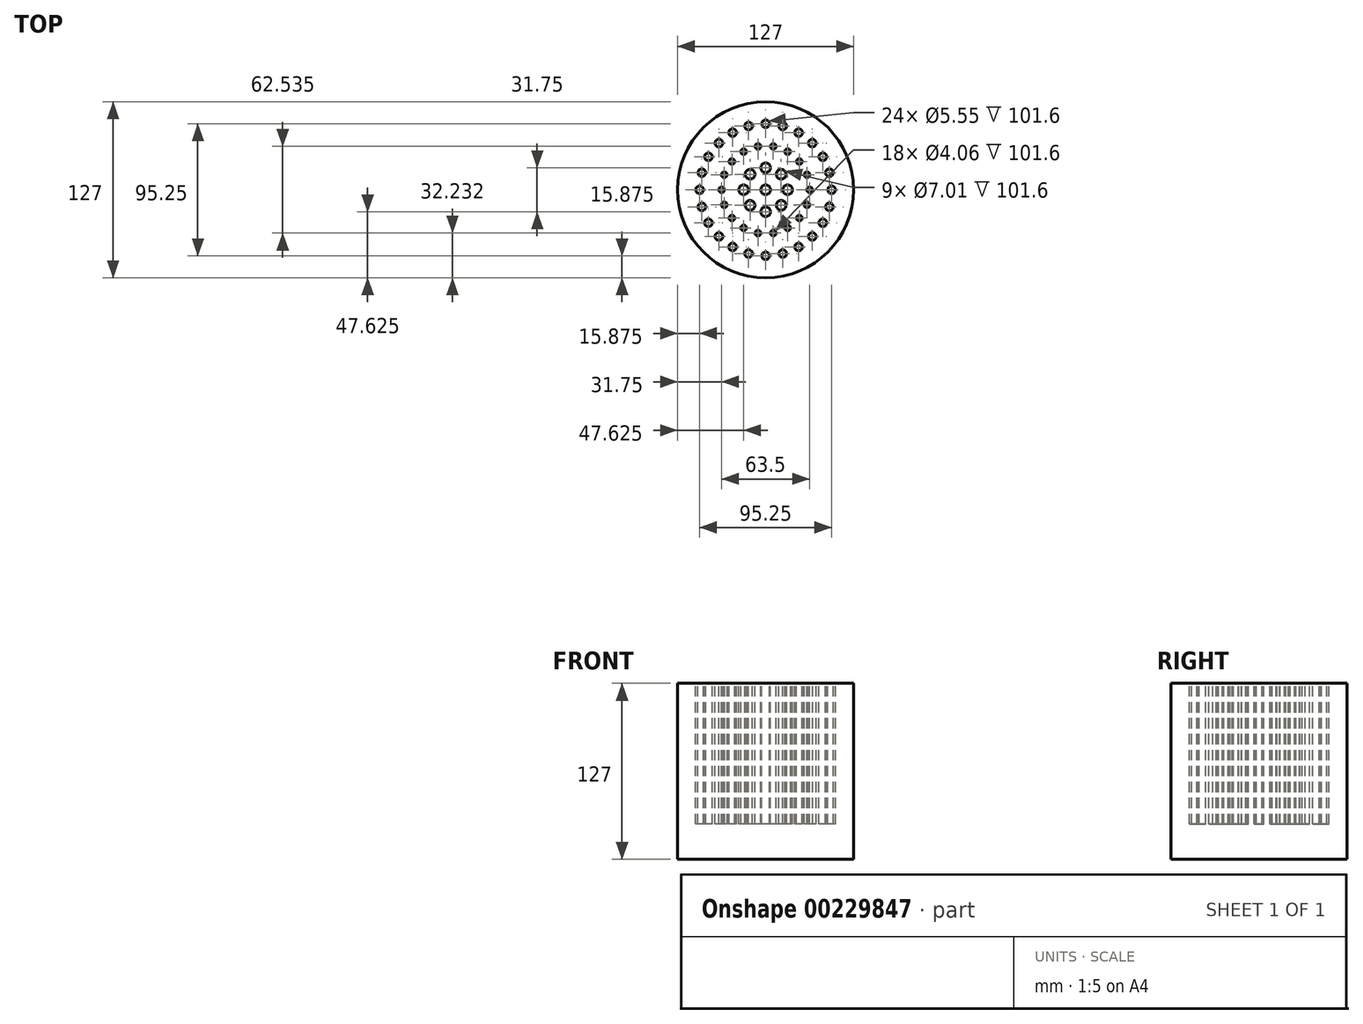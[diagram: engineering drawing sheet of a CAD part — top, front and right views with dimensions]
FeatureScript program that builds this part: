
annotation { "Feature Type Name" : "Feature", "Feature Type Description" : "" }
export const myFeature = defineFeature(function(context is Context, id is Id, definition is map)
    precondition{}
    {
        {
            var Q0;
            Q0=qCreatedBy(makeId("Top.planeOp"),FACE);
            var sketch = newSketch(context, id + "F0", { "sketchPlane" : qUnion([Q0])});
            skCircle(sketch, "E0", {"center": v(0, 0) * mm, "radius": 63.5 * mm});
            skSolve(sketch);
        }
        {
            var Q0;
            Q0 = qSketchRegion(id + "F0", true);
            extrude(context, id + "F1", {"entities" : qUnion([Q0]), "endBound" : BoundingType.SYMMETRIC, "depth" : 127 * mm});
        }
        {
            var Q0;
            Q0=makeQuery(id+"F1.opExtrude","CAP_FACE",FACE,{"disambiguationData":[OSD([sQuery(id+"F0.wireOp",EDGE,"E0")])],"isStart":false});
            var sketch = newSketch(context, id + "F2", { "sketchPlane" : qUnion([Q0])});
            skCircle(sketch, "E1", {"center": v(0, 0) * mm, "radius": 3.5 * mm});
            skLineSegment(sketch, "E2", {"start": v(0, 0) * mm, "end": v(-15.88, 0) * mm});
            skLineSegment(sketch, "E3", {"start": v(-15.88, 0) * mm, "end": v(-31.75, 0) * mm});
            skLineSegment(sketch, "E4", {"start": v(-31.75, 0) * mm, "end": v(-47.62, 0) * mm});
            skCircle(sketch, "E5", {"center": v(-47.62, 0) * mm, "radius": 2.78 * mm});
            skCircle(sketch, "E6.1.0", {"center": v(-46, -12.33) * mm, "radius": 2.78 * mm});
            skCircle(sketch, "E6.2.0", {"center": v(-41.24, -23.81) * mm, "radius": 2.78 * mm});
            skCircle(sketch, "E6.3.0", {"center": v(-33.68, -33.68) * mm, "radius": 2.78 * mm});
            skCircle(sketch, "E6.4.0", {"center": v(-23.81, -41.24) * mm, "radius": 2.78 * mm});
            skCircle(sketch, "E6.5.0", {"center": v(-12.33, -46) * mm, "radius": 2.78 * mm});
            skCircle(sketch, "E6.6.0", {"center": v(0, -47.62) * mm, "radius": 2.78 * mm});
            skCircle(sketch, "E6.7.0", {"center": v(12.33, -46) * mm, "radius": 2.78 * mm});
            skCircle(sketch, "E6.8.0", {"center": v(23.81, -41.24) * mm, "radius": 2.78 * mm});
            skCircle(sketch, "E6.9.0", {"center": v(33.68, -33.68) * mm, "radius": 2.78 * mm});
            skCircle(sketch, "E6.10.0", {"center": v(41.24, -23.81) * mm, "radius": 2.78 * mm});
            skCircle(sketch, "E6.11.0", {"center": v(46, -12.33) * mm, "radius": 2.78 * mm});
            skCircle(sketch, "E6.12.0", {"center": v(47.63, 0) * mm, "radius": 2.78 * mm});
            skCircle(sketch, "E6.13.0", {"center": v(46, 12.33) * mm, "radius": 2.78 * mm});
            skCircle(sketch, "E6.14.0", {"center": v(41.24, 23.81) * mm, "radius": 2.78 * mm});
            skCircle(sketch, "E6.15.0", {"center": v(33.68, 33.68) * mm, "radius": 2.78 * mm});
            skCircle(sketch, "E6.16.0", {"center": v(23.81, 41.24) * mm, "radius": 2.78 * mm});
            skCircle(sketch, "E6.17.0", {"center": v(12.33, 46) * mm, "radius": 2.78 * mm});
            skCircle(sketch, "E6.18.0", {"center": v(0, 47.62) * mm, "radius": 2.78 * mm});
            skCircle(sketch, "E6.19.0", {"center": v(-12.33, 46) * mm, "radius": 2.78 * mm});
            skCircle(sketch, "E7.1.20.0", {"center": v(-23.81, 41.24) * mm, "radius": 2.78 * mm});
            skCircle(sketch, "E7.1.21.0", {"center": v(-33.68, 33.68) * mm, "radius": 2.78 * mm});
            skCircle(sketch, "E7.1.22.0", {"center": v(-41.24, 23.81) * mm, "radius": 2.78 * mm});
            skCircle(sketch, "E7.1.23.0", {"center": v(-46, 12.33) * mm, "radius": 2.78 * mm});
            skCircle(sketch, "E8", {"center": v(-31.75, 0) * mm, "radius": 2.03 * mm});
            skCircle(sketch, "E9.1.0", {"center": v(-29.84, -10.86) * mm, "radius": 2.03 * mm});
            skCircle(sketch, "E9.2.0", {"center": v(-24.32, -20.4) * mm, "radius": 2.03 * mm});
            skCircle(sketch, "E9.3.0", {"center": v(-15.88, -27.5) * mm, "radius": 2.03 * mm});
            skCircle(sketch, "E9.4.0", {"center": v(-5.51, -31.27) * mm, "radius": 2.03 * mm});
            skCircle(sketch, "E9.5.0", {"center": v(5.51, -31.27) * mm, "radius": 2.03 * mm});
            skCircle(sketch, "E9.6.0", {"center": v(15.87, -27.5) * mm, "radius": 2.03 * mm});
            skCircle(sketch, "E9.7.0", {"center": v(24.32, -20.4) * mm, "radius": 2.03 * mm});
            skCircle(sketch, "E9.8.0", {"center": v(29.84, -10.86) * mm, "radius": 2.03 * mm});
            skCircle(sketch, "E9.9.0", {"center": v(31.75, 0) * mm, "radius": 2.03 * mm});
            skCircle(sketch, "E9.10.0", {"center": v(29.84, 10.86) * mm, "radius": 2.03 * mm});
            skCircle(sketch, "E9.11.0", {"center": v(24.32, 20.4) * mm, "radius": 2.03 * mm});
            skCircle(sketch, "E9.12.0", {"center": v(15.88, 27.5) * mm, "radius": 2.03 * mm});
            skCircle(sketch, "E9.13.0", {"center": v(5.51, 31.27) * mm, "radius": 2.03 * mm});
            skCircle(sketch, "E9.14.0", {"center": v(-5.51, 31.27) * mm, "radius": 2.03 * mm});
            skCircle(sketch, "E9.15.0", {"center": v(-15.87, 27.5) * mm, "radius": 2.03 * mm});
            skCircle(sketch, "E9.16.0", {"center": v(-24.32, 20.4) * mm, "radius": 2.03 * mm});
            skCircle(sketch, "E9.17.0", {"center": v(-29.84, 10.86) * mm, "radius": 2.03 * mm});
            skCircle(sketch, "E10", {"center": v(-15.88, 0) * mm, "radius": 3.5 * mm});
            skCircle(sketch, "E11.1.0", {"center": v(-11.23, -11.23) * mm, "radius": 3.5 * mm});
            skCircle(sketch, "E11.2.0", {"center": v(0, -15.88) * mm, "radius": 3.5 * mm});
            skCircle(sketch, "E11.3.0", {"center": v(11.23, -11.23) * mm, "radius": 3.5 * mm});
            skCircle(sketch, "E11.4.0", {"center": v(15.88, 0) * mm, "radius": 3.5 * mm});
            skCircle(sketch, "E11.5.0", {"center": v(11.23, 11.23) * mm, "radius": 3.5 * mm});
            skCircle(sketch, "E11.6.0", {"center": v(0, 15.88) * mm, "radius": 3.5 * mm});
            skCircle(sketch, "E11.7.0", {"center": v(-11.23, 11.23) * mm, "radius": 3.5 * mm});
            skSolve(sketch);
        }
        {
            var Q0;
            Q0 = qSketchRegion(id + "F2", true);
            extrude(context, id + "F3", {"entities" : qUnion([Q0]), "operationType" : NewBodyOperationType.REMOVE, "oppositeDirection" : true, "depth" : 101.6 * mm});
        }
    });
